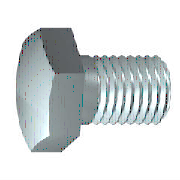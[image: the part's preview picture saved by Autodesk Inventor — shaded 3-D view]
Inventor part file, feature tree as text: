
AUTODESK INVENTOR PART (.ipt)
format: ipt  version: 2018.1 (Build 221171000, 171)  size: 193,024 bytes
history: native  units: mm (DEFAULTED — no unit token found)
features: sketch x4, extrude x2, chamfer x1, plane x1
ambient origin geometry x7: Origin, YZ Plane, XZ Plane, X Axis, Y Axis, Z Axis, Center Point
bodies: Solid1 (feature_tree), Body (feature_tree)
feature tree (8):
  extrude  "Head"  Depth=12.0mm
  extrude  "Indent"  Depth=9.0mm
  chamfer  "Chamfer1"  Angle=90.0deg  [1 undecoded]
  plane  "Work Plane1"
  sketch  "Sketch1"  dims[d0=38.0mm d1=12.0mm]
  sketch  "Sketch2"  dims[d12=90.0deg d2=9.0mm]
  sketch  "Sketch4"  dims[d4=30.0deg d21=90.0deg d5=1.55mm d6=1.073638mm d7=0.0mm d8=18.0mm d9=38.0mm d10=0.0mm d13=70.0mm d14=1.073538mm d16=10.68mm d17=18.0mm d18=0.0001mm d19=0.001mm d20=0.0mm d77=45.0deg d79=0.0mm d80=0.0mm]
  sketch  "Sketch3"  dims[d3=0.0mm]
note: 1 required parameter value undecoded (feature->parameter linkage not recoverable at this tier; creation-order binding heuristic only, values carry confidence <= 0.55)
